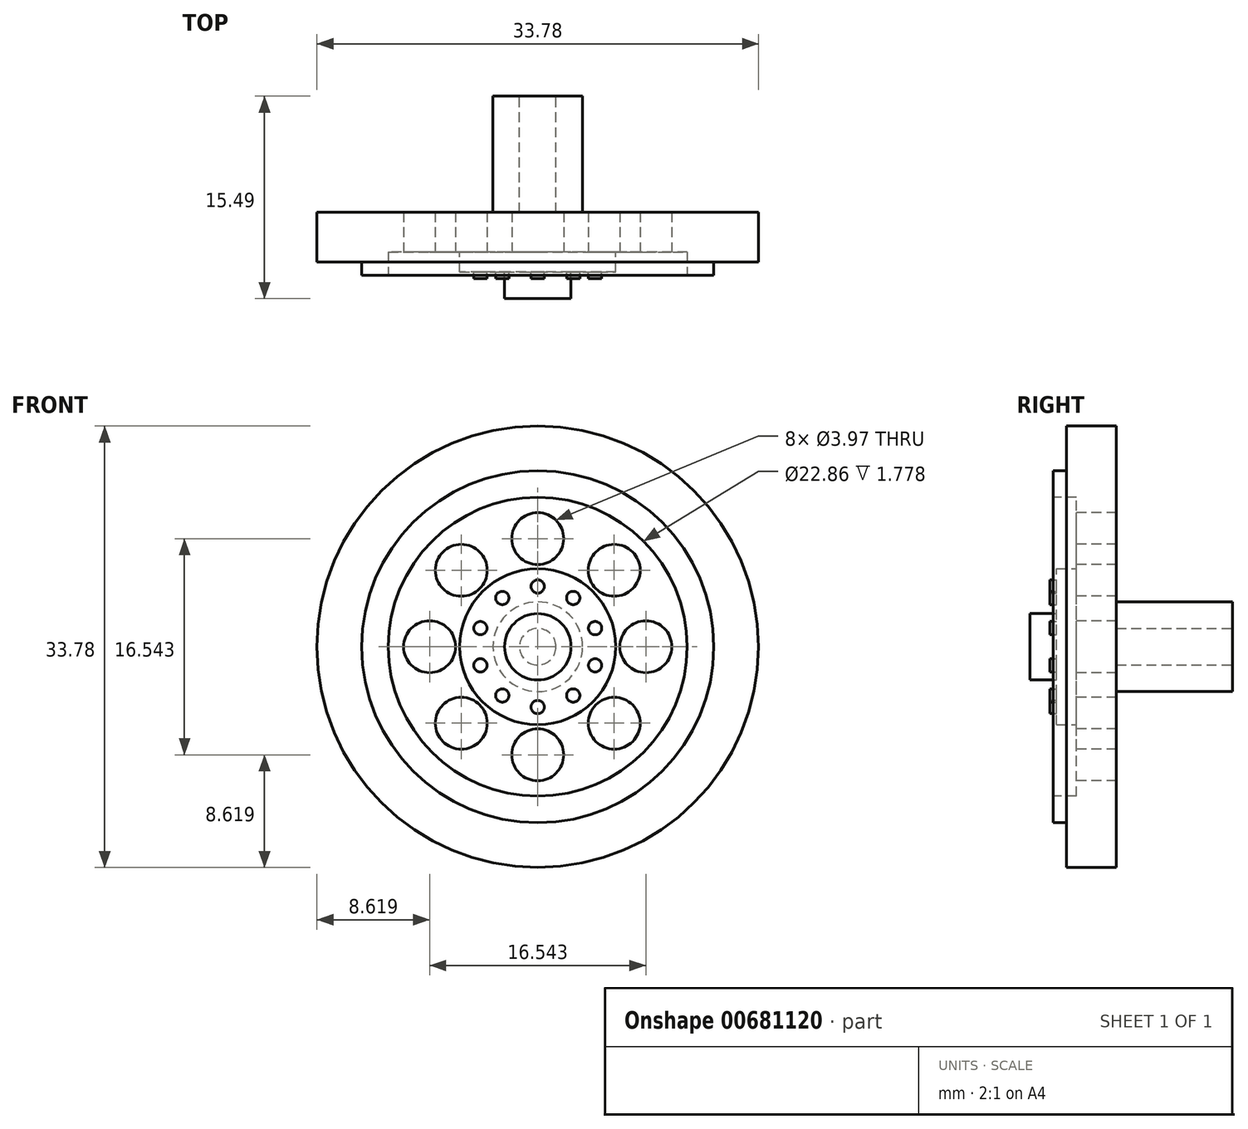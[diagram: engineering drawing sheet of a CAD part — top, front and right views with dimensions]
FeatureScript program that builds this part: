
annotation { "Feature Type Name" : "Feature", "Feature Type Description" : "" }
export const myFeature = defineFeature(function(context is Context, id is Id, definition is map)
    precondition{}
    {
        {
            var Q0;
            Q0=qCreatedBy(makeId("Front.planeOp"),FACE);
            var sketch = newSketch(context, id + "F0", { "sketchPlane" : qUnion([Q0])});
            skCircle(sketch, "E0", {"center": v(0, 0) * mm, "radius": 16.9 * mm});
            skSolve(sketch);
        }
        {
            var Q0;
            Q0=makeQuery(id+"F0.imprint","IMPRINT",FACE,{"disambiguationData":[TD([[makeQuery(id+"F0.imprint","IMPRINT",EDGE,{"derivedFrom":sQuery(id+"F0.wireOp",EDGE,"E0")}),1.0]])]});
            var sketch = newSketch(context, id + "F1", { "sketchPlane" : qUnion([Q0])});
            skCircle(sketch, "E1", {"center": v(0, 0) * mm, "radius": 13.46 * mm});
            skSolve(sketch);
        }
        {
            var Q0;
            Q0=makeQuery(id+"F0.imprint","IMPRINT",FACE,{"disambiguationData":[TD([[makeQuery(id+"F0.imprint","IMPRINT",EDGE,{"derivedFrom":sQuery(id+"F0.wireOp",EDGE,"E0")}),1.0]])]});
            extrude(context, id + "F2", {"entities" : qUnion([Q0]), "oppositeDirection" : true, "depth" : 3.8 * mm, "offsetDistance" : 25.4 * mm});
        }
        {
            var Q0;
            Q0=makeQuery(id+"F1.imprint","IMPRINT",FACE,{"disambiguationData":[TD([[makeQuery(id+"F1.imprint","IMPRINT",EDGE,{"derivedFrom":sQuery(id+"F1.wireOp",EDGE,"E1")}),1.0]])]});
            extrude(context, id + "F3", {"entities" : qUnion([Q0]), "operationType" : NewBodyOperationType.ADD, "depth" : 1.02 * mm, "offsetDistance" : 25.4 * mm});
        }
        {
            var Q0;
            Q0=makeQuery(id+"F3.opExtrude","CAP_FACE",FACE,{"disambiguationData":[OSD([sQuery(id+"F1.wireOp",EDGE,"E1")])],"isStart":false});
            var sketch = newSketch(context, id + "F4", { "sketchPlane" : qUnion([Q0])});
            skCircle(sketch, "E2", {"center": v(0, 0) * mm, "radius": 11.43 * mm});
            skSolve(sketch);
        }
        {
            var Q0;
            Q0=makeQuery(id+"F4.imprint","IMPRINT",FACE,{"disambiguationData":[TD([[makeQuery(id+"F4.imprint","IMPRINT",EDGE,{"derivedFrom":sQuery(id+"F4.wireOp",EDGE,"E2")}),1.0]])]});
            extrude(context, id + "F5", {"entities" : qUnion([Q0]), "operationType" : NewBodyOperationType.REMOVE, "oppositeDirection" : true, "depth" : 1.78 * mm, "offsetDistance" : 25.4 * mm});
        }
        {
            var Q0;
            Q0=makeQuery(id+"F5.boolean.opBoolean","COPY",FACE,{"derivedFrom":makeQuery(id+"F5.opExtrude","CAP_FACE",FACE,{"disambiguationData":[OSD([sQuery(id+"F4.wireOp",EDGE,"E2")])],"isStart":false})});
            var sketch = newSketch(context, id + "F6", { "sketchPlane" : qUnion([Q0])});
            skCircle(sketch, "E3", {"center": v(0, 8.27) * mm, "radius": 1.99 * mm});
            skCircle(sketch, "E4.1.0", {"center": v(-5.85, 5.85) * mm, "radius": 1.99 * mm});
            skCircle(sketch, "E4.2.0", {"center": v(-8.27, 0) * mm, "radius": 1.99 * mm});
            skCircle(sketch, "E4.3.0", {"center": v(-5.85, -5.85) * mm, "radius": 1.99 * mm});
            skCircle(sketch, "E4.4.0", {"center": v(0, -8.27) * mm, "radius": 1.99 * mm});
            skCircle(sketch, "E4.5.0", {"center": v(5.85, -5.85) * mm, "radius": 1.99 * mm});
            skCircle(sketch, "E4.6.0", {"center": v(8.27, 0) * mm, "radius": 1.99 * mm});
            skCircle(sketch, "E4.7.0", {"center": v(5.85, 5.85) * mm, "radius": 1.99 * mm});
            skPoint(sketch, "E4.center", {"position": v(0, 0) * mm});
            skSolve(sketch);
        }
        {
            var Q0;
            Q0=makeQuery(id+"F6.imprint","IMPRINT",FACE,{"disambiguationData":[TD([[makeQuery(id+"F6.imprint","IMPRINT",EDGE,{"derivedFrom":sQuery(id+"F6.wireOp",EDGE,"E3")}),1.0]])]});
            var Q1;
            Q1=makeQuery(id+"F6.imprint","IMPRINT",FACE,{"disambiguationData":[TD([[makeQuery(id+"F6.imprint","IMPRINT",EDGE,{"derivedFrom":sQuery(id+"F6.wireOp",EDGE,"E4.7.0")}),1.0]])]});
            var Q2;
            Q2=makeQuery(id+"F6.imprint","IMPRINT",FACE,{"disambiguationData":[TD([[makeQuery(id+"F6.imprint","IMPRINT",EDGE,{"derivedFrom":sQuery(id+"F6.wireOp",EDGE,"E4.6.0")}),1.0]])]});
            var Q3;
            Q3=makeQuery(id+"F6.imprint","IMPRINT",FACE,{"disambiguationData":[TD([[makeQuery(id+"F6.imprint","IMPRINT",EDGE,{"derivedFrom":sQuery(id+"F6.wireOp",EDGE,"E4.5.0")}),1.0]])]});
            var Q4;
            Q4=makeQuery(id+"F6.imprint","IMPRINT",FACE,{"disambiguationData":[TD([[makeQuery(id+"F6.imprint","IMPRINT",EDGE,{"derivedFrom":sQuery(id+"F6.wireOp",EDGE,"E4.4.0")}),1.0]])]});
            var Q5;
            Q5=makeQuery(id+"F6.imprint","IMPRINT",FACE,{"disambiguationData":[TD([[makeQuery(id+"F6.imprint","IMPRINT",EDGE,{"derivedFrom":sQuery(id+"F6.wireOp",EDGE,"E4.3.0")}),1.0]])]});
            var Q6;
            Q6=makeQuery(id+"F6.imprint","IMPRINT",FACE,{"disambiguationData":[TD([[makeQuery(id+"F6.imprint","IMPRINT",EDGE,{"derivedFrom":sQuery(id+"F6.wireOp",EDGE,"E4.2.0")}),1.0]])]});
            var Q7;
            Q7=makeQuery(id+"F6.imprint","IMPRINT",FACE,{"disambiguationData":[TD([[makeQuery(id+"F6.imprint","IMPRINT",EDGE,{"derivedFrom":sQuery(id+"F6.wireOp",EDGE,"E4.1.0")}),1.0]])]});
            extrude(context, id + "F7", {"entities" : qUnion([Q0, Q1, Q2, Q3, Q4, Q5, Q6, Q7]), "operationType" : NewBodyOperationType.REMOVE, "oppositeDirection" : true, "depth" : 25.4 * mm, "offsetDistance" : 25.4 * mm});
        }
        {
            var Q0;
            Q0=makeQuery(id+"F5.boolean.opBoolean","COPY",FACE,{"derivedFrom":makeQuery(id+"F5.opExtrude","CAP_FACE",FACE,{"disambiguationData":[OSD([sQuery(id+"F4.wireOp",EDGE,"E2")])],"isStart":false})});
            var sketch = newSketch(context, id + "F8", { "sketchPlane" : qUnion([Q0])});
            skCircle(sketch, "E5", {"center": v(0, 0) * mm, "radius": 5.97 * mm});
            skSolve(sketch);
        }
        {
            var Q0;
            Q0=makeQuery(id+"F8.imprint","IMPRINT",FACE,{"disambiguationData":[TD([[makeQuery(id+"F8.imprint","IMPRINT",EDGE,{"derivedFrom":sQuery(id+"F8.wireOp",EDGE,"E5")}),1.0]])]});
            extrude(context, id + "F9", {"entities" : qUnion([Q0]), "operationType" : NewBodyOperationType.ADD, "depth" : 1.52 * mm, "offsetDistance" : 25.4 * mm});
        }
        {
            var Q0;
            Q0=makeQuery(id+"F9.opExtrude","CAP_FACE",FACE,{"disambiguationData":[OSD([sQuery(id+"F8.wireOp",EDGE,"E5")])],"isStart":false});
            var sketch = newSketch(context, id + "F10", { "sketchPlane" : qUnion([Q0])});
            skCircle(sketch, "E6", {"center": v(0, 4.61) * mm, "radius": 0.5 * mm});
            skCircle(sketch, "E7.1.0", {"center": v(-2.71, 3.73) * mm, "radius": 0.5 * mm});
            skCircle(sketch, "E7.2.0", {"center": v(-4.39, 1.43) * mm, "radius": 0.5 * mm});
            skCircle(sketch, "E7.3.0", {"center": v(-4.39, -1.43) * mm, "radius": 0.5 * mm});
            skCircle(sketch, "E7.4.0", {"center": v(-2.71, -3.73) * mm, "radius": 0.5 * mm});
            skCircle(sketch, "E7.5.0", {"center": v(0, -4.61) * mm, "radius": 0.5 * mm});
            skCircle(sketch, "E7.6.0", {"center": v(2.71, -3.73) * mm, "radius": 0.5 * mm});
            skCircle(sketch, "E7.7.0", {"center": v(4.39, -1.43) * mm, "radius": 0.5 * mm});
            skCircle(sketch, "E7.8.0", {"center": v(4.39, 1.43) * mm, "radius": 0.5 * mm});
            skCircle(sketch, "E7.9.0", {"center": v(2.71, 3.73) * mm, "radius": 0.5 * mm});
            skPoint(sketch, "E7.center", {"position": v(0, 0) * mm});
            skSolve(sketch);
        }
        {
            var Q0;
            Q0=makeQuery(id+"F10.imprint","IMPRINT",FACE,{"disambiguationData":[TD([[makeQuery(id+"F10.imprint","IMPRINT",EDGE,{"derivedFrom":sQuery(id+"F10.wireOp",EDGE,"E7.1.0")}),1.0]])]});
            var Q1;
            Q1=makeQuery(id+"F10.imprint","IMPRINT",FACE,{"disambiguationData":[TD([[makeQuery(id+"F10.imprint","IMPRINT",EDGE,{"derivedFrom":sQuery(id+"F10.wireOp",EDGE,"E6")}),1.0]])]});
            var Q2;
            Q2=makeQuery(id+"F10.imprint","IMPRINT",FACE,{"disambiguationData":[TD([[makeQuery(id+"F10.imprint","IMPRINT",EDGE,{"derivedFrom":sQuery(id+"F10.wireOp",EDGE,"E7.9.0")}),1.0]])]});
            var Q3;
            Q3=makeQuery(id+"F10.imprint","IMPRINT",FACE,{"disambiguationData":[TD([[makeQuery(id+"F10.imprint","IMPRINT",EDGE,{"derivedFrom":sQuery(id+"F10.wireOp",EDGE,"E7.8.0")}),1.0]])]});
            var Q4;
            Q4=makeQuery(id+"F10.imprint","IMPRINT",FACE,{"disambiguationData":[TD([[makeQuery(id+"F10.imprint","IMPRINT",EDGE,{"derivedFrom":sQuery(id+"F10.wireOp",EDGE,"E7.7.0")}),1.0]])]});
            var Q5;
            Q5=makeQuery(id+"F10.imprint","IMPRINT",FACE,{"disambiguationData":[TD([[makeQuery(id+"F10.imprint","IMPRINT",EDGE,{"derivedFrom":sQuery(id+"F10.wireOp",EDGE,"E7.6.0")}),1.0]])]});
            var Q6;
            Q6=makeQuery(id+"F10.imprint","IMPRINT",FACE,{"disambiguationData":[TD([[makeQuery(id+"F10.imprint","IMPRINT",EDGE,{"derivedFrom":sQuery(id+"F10.wireOp",EDGE,"E7.5.0")}),1.0]])]});
            var Q7;
            Q7=makeQuery(id+"F10.imprint","IMPRINT",FACE,{"disambiguationData":[TD([[makeQuery(id+"F10.imprint","IMPRINT",EDGE,{"derivedFrom":sQuery(id+"F10.wireOp",EDGE,"E7.4.0")}),1.0]])]});
            var Q8;
            Q8=makeQuery(id+"F10.imprint","IMPRINT",FACE,{"disambiguationData":[TD([[makeQuery(id+"F10.imprint","IMPRINT",EDGE,{"derivedFrom":sQuery(id+"F10.wireOp",EDGE,"E7.3.0")}),1.0]])]});
            var Q9;
            Q9=makeQuery(id+"F10.imprint","IMPRINT",FACE,{"disambiguationData":[TD([[makeQuery(id+"F10.imprint","IMPRINT",EDGE,{"derivedFrom":sQuery(id+"F10.wireOp",EDGE,"E7.2.0")}),1.0]])]});
            extrude(context, id + "F11", {"entities" : qUnion([Q0, Q1, Q2, Q3, Q4, Q5, Q6, Q7, Q8, Q9]), "operationType" : NewBodyOperationType.ADD, "depth" : 0.5 * mm, "offsetDistance" : 25.4 * mm});
        }
        {
            var Q0;
            Q0=makeQuery(id+"F9.opExtrude","CAP_FACE",FACE,{"disambiguationData":[OSD([sQuery(id+"F8.wireOp",EDGE,"E5")])],"isStart":false});
            var sketch = newSketch(context, id + "F12", { "sketchPlane" : qUnion([Q0])});
            skCircle(sketch, "E8", {"center": v(0, 0) * mm, "radius": 2.54 * mm});
            skSolve(sketch);
        }
        {
            var Q0;
            Q0=makeQuery(id+"F12.imprint","IMPRINT",FACE,{"disambiguationData":[TD([[makeQuery(id+"F12.imprint","IMPRINT",EDGE,{"derivedFrom":sQuery(id+"F12.wireOp",EDGE,"E8")}),1.0]])]});
            extrude(context, id + "F13", {"entities" : qUnion([Q0]), "operationType" : NewBodyOperationType.ADD, "depth" : 2.03 * mm, "offsetDistance" : 25.4 * mm});
        }
        {
            var Q0;
            Q0=makeQuery(id+"F2.opExtrude","CAP_FACE",FACE,{"disambiguationData":[OSD([sQuery(id+"F0.wireOp",EDGE,"E0")])],"isStart":false});
            var sketch = newSketch(context, id + "F14", { "sketchPlane" : qUnion([Q0])});
            skCircle(sketch, "E9", {"center": v(0, 0) * mm, "radius": 3.43 * mm});
            skSolve(sketch);
        }
        {
            var Q0;
            Q0=makeQuery(id+"F14.imprint","IMPRINT",FACE,{"disambiguationData":[TD([[makeQuery(id+"F14.imprint","IMPRINT",EDGE,{"derivedFrom":sQuery(id+"F14.wireOp",EDGE,"E9")}),1.0]])]});
            extrude(context, id + "F15", {"entities" : qUnion([Q0]), "depth" : 8.9 * mm, "offsetDistance" : 25.4 * mm});
        }
        {
            var Q0;
            Q0=makeQuery(id+"F15.opExtrude","CAP_FACE",FACE,{"disambiguationData":[OSD([sQuery(id+"F14.wireOp",EDGE,"E9")])],"isStart":false});
            var sketch = newSketch(context, id + "F16", { "sketchPlane" : qUnion([Q0])});
            skCircle(sketch, "E10", {"center": v(0, 0) * mm, "radius": 1.4 * mm});
            skSolve(sketch);
        }
        {
            var Q0;
            Q0=makeQuery(id+"F16.imprint","IMPRINT",FACE,{"disambiguationData":[TD([[makeQuery(id+"F16.imprint","IMPRINT",EDGE,{"derivedFrom":sQuery(id+"F16.wireOp",EDGE,"E10")}),1.0]])]});
            extrude(context, id + "F17", {"entities" : qUnion([Q0]), "operationType" : NewBodyOperationType.REMOVE, "oppositeDirection" : true, "depth" : 8.9 * mm, "offsetDistance" : 25.4 * mm});
        }
    });
